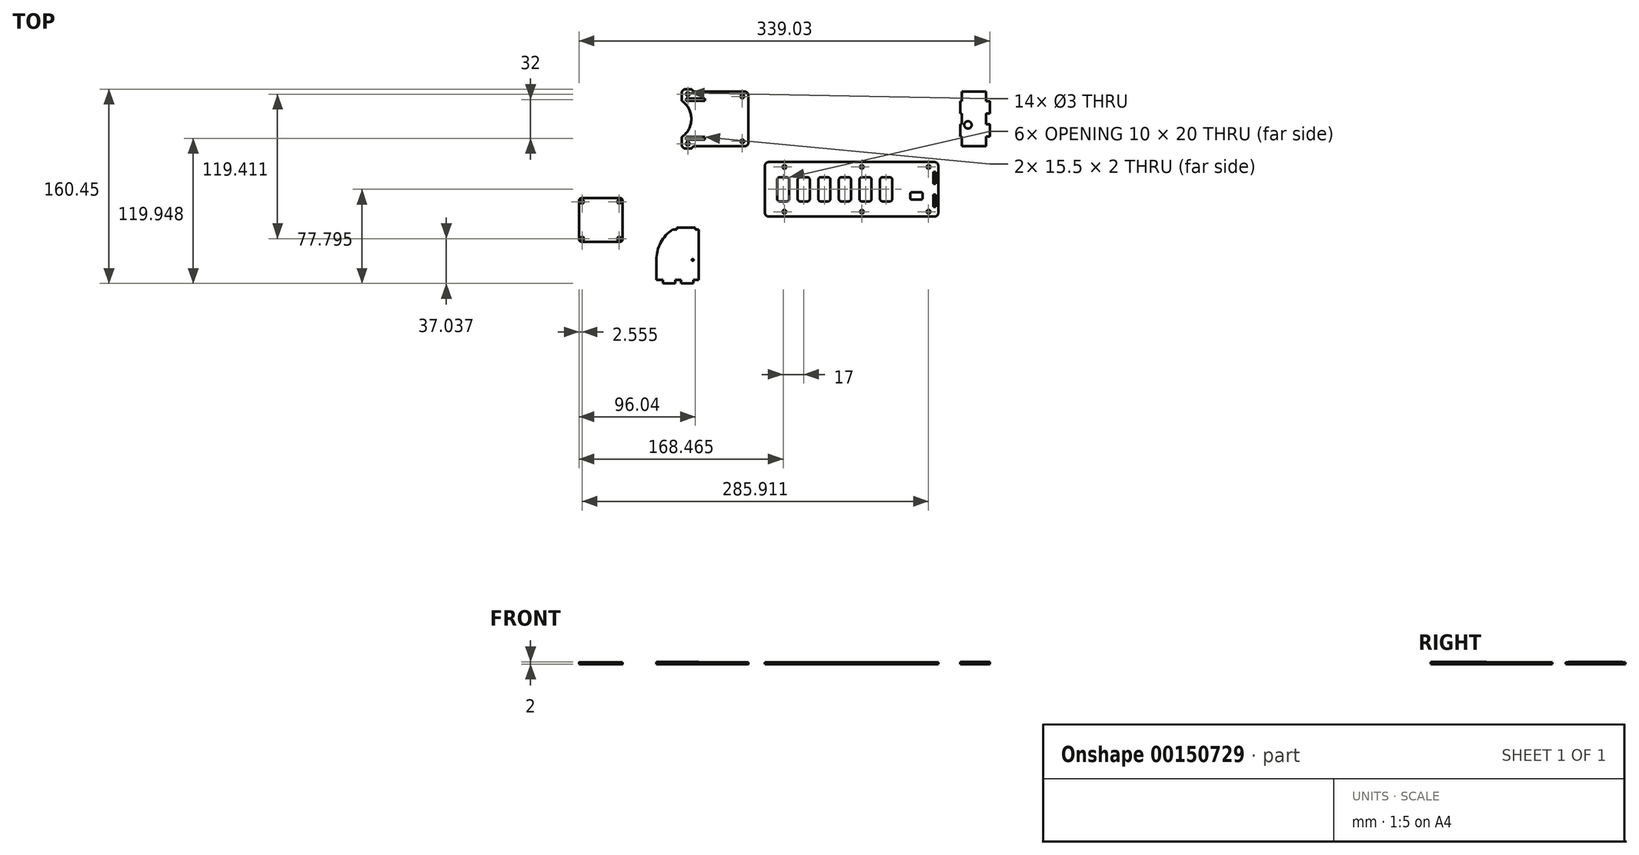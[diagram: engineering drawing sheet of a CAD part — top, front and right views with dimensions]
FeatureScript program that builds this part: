
annotation { "Feature Type Name" : "Feature", "Feature Type Description" : "" }
export const myFeature = defineFeature(function(context is Context, id is Id, definition is map)
    precondition{}
    {
        {
            var Q0;
            Q0=qCreatedBy(makeId("Top.planeOp"),FACE);
            var sketch = newSketch(context, id + "F0", { "sketchPlane" : qUnion([Q0])});
            skLineSegment(sketch, "E0", {"start": v(29.73, 71.96) * mm, "end": v(20.47, 71.96) * mm, "construction": true});
            skPoint(sketch, "E0.startSnap0", {"position": v(35, 71.96) * mm});
            skLineSegment(sketch, "E1.bottom", {"start": v(-69.79, 6.5) * mm, "end": v(-37.79, 6.5) * mm});
            skLineSegment(sketch, "E1.top", {"start": v(-69.79, -29.5) * mm, "end": v(-37.79, -29.5) * mm});
            skLineSegment(sketch, "E1.left", {"start": v(-71.79, 4.5) * mm, "end": v(-71.79, -27.5) * mm});
            skLineSegment(sketch, "E1.right", {"start": v(-35.79, 4.5) * mm, "end": v(-35.79, -27.5) * mm});
            skLineSegment(sketch, "E2.bottom", {"start": v(-69.24, 3.55) * mm, "end": v(-38.74, 3.55) * mm, "construction": true});
            skLineSegment(sketch, "E2.top", {"start": v(-69.24, -26.95) * mm, "end": v(-38.74, -26.95) * mm, "construction": true});
            skLineSegment(sketch, "E2.left", {"start": v(-69.24, 3.55) * mm, "end": v(-69.24, -26.95) * mm, "construction": true});
            skLineSegment(sketch, "E2.right", {"start": v(-38.74, 3.55) * mm, "end": v(-38.74, -26.95) * mm, "construction": true});
            skCircle(sketch, "E3", {"center": v(-69.24, 3.55) * mm, "radius": 1.5 * mm});
            skCircle(sketch, "E4", {"center": v(-38.74, 3.55) * mm, "radius": 1.5 * mm});
            skCircle(sketch, "E5", {"center": v(-38.74, -26.95) * mm, "radius": 1.5 * mm});
            skCircle(sketch, "E6", {"center": v(-69.24, -26.95) * mm, "radius": 1.5 * mm});
            skPoint(sketch, "E7.visualSharp", {"position": v(-71.79, 6.5) * mm});
            skArc(sketch, "E7.filletArc", {"start": v(-69.79, 6.5) * mm, "mid": v(-71.2, 5.91) * mm, "end": v(-71.79, 4.5) * mm});
            skPoint(sketch, "E8.visualSharp", {"position": v(-35.79, 6.5) * mm});
            skArc(sketch, "E8.filletArc", {"start": v(-35.79, 4.5) * mm, "mid": v(-36.37, 5.91) * mm, "end": v(-37.79, 6.5) * mm});
            skPoint(sketch, "E9.visualSharp", {"position": v(-35.79, -29.5) * mm});
            skArc(sketch, "E9.filletArc", {"start": v(-37.79, -29.5) * mm, "mid": v(-36.37, -28.92) * mm, "end": v(-35.79, -27.5) * mm});
            skPoint(sketch, "E10.visualSharp", {"position": v(-71.79, -29.5) * mm});
            skArc(sketch, "E10.filletArc", {"start": v(-71.79, -27.5) * mm, "mid": v(-71.2, -28.92) * mm, "end": v(-69.79, -29.5) * mm});
            skLineSegment(sketch, "E11", {"start": v(32, 54.96) * mm, "end": v(16.5, 54.96) * mm});
            skLineSegment(sketch, "E12", {"start": v(16.5, 54.96) * mm, "end": v(16.5, 56.96) * mm});
            skLineSegment(sketch, "E13", {"start": v(16.5, 56.96) * mm, "end": v(32, 56.96) * mm});
            skLineSegment(sketch, "E14", {"start": v(32, 56.96) * mm, "end": v(32, 54.96) * mm});
            skLineSegment(sketch, "E15.MirrorCS", {"start": v(32, 86.96) * mm, "end": v(32, 88.96) * mm});
            skLineSegment(sketch, "E16.MirrorCS", {"start": v(16.5, 86.96) * mm, "end": v(32, 86.96) * mm});
            skLineSegment(sketch, "E17.MirrorCS", {"start": v(16.5, 88.96) * mm, "end": v(16.5, 86.96) * mm});
            skLineSegment(sketch, "E18.MirrorCS", {"start": v(32, 88.96) * mm, "end": v(16.5, 88.96) * mm});
            skLineSegment(sketch, "E19", {"start": v(13, 94.46) * mm, "end": v(13, 86.96) * mm});
            skLineSegment(sketch, "E20", {"start": v(13, 49.46) * mm, "end": v(13, 56.96) * mm});
            skArc(sketch, "E21", {"start": v(13, 56.96) * mm, "mid": v(20.87, 71.96) * mm, "end": v(13, 86.96) * mm});
            skLineSegment(sketch, "E22.bottom", {"start": v(244.24, 94.46) * mm, "end": v(264.24, 94.46) * mm});
            skLineSegment(sketch, "E22.top", {"start": v(244.24, 49.46) * mm, "end": v(264.24, 49.46) * mm});
            skLineSegment(sketch, "E22.left", {"start": v(244.24, 94.46) * mm, "end": v(244.24, 49.46) * mm});
            skLineSegment(sketch, "E22.right", {"start": v(264.24, 94.46) * mm, "end": v(264.24, 49.46) * mm});
            skLineSegment(sketch, "E23", {"start": v(244.24, 86.46) * mm, "end": v(242.74, 86.46) * mm});
            skLineSegment(sketch, "E24", {"start": v(242.74, 57.46) * mm, "end": v(244.24, 57.46) * mm});
            skLineSegment(sketch, "E25", {"start": v(254.24, 80.62) * mm, "end": v(254.24, 71.6) * mm, "construction": true});
            skPoint(sketch, "E25.startSnap0", {"position": v(254.24, 94.46) * mm});
            skLineSegment(sketch, "E26", {"start": v(252.37, 71.96) * mm, "end": v(257.45, 71.96) * mm, "construction": true});
            skPoint(sketch, "E26.startSnap0", {"position": v(244.24, 71.96) * mm});
            skCircle(sketch, "E27", {"center": v(249.24, 66.96) * mm, "radius": 3.05 * mm});
            skLineSegment(sketch, "E28", {"start": v(242.74, 86.46) * mm, "end": v(242.74, 76.46) * mm});
            skLineSegment(sketch, "E29", {"start": v(242.74, 76.46) * mm, "end": v(244.24, 76.46) * mm});
            skLineSegment(sketch, "E30", {"start": v(242.74, 57.46) * mm, "end": v(242.74, 67.46) * mm});
            skLineSegment(sketch, "E31", {"start": v(242.74, 67.46) * mm, "end": v(244.24, 67.46) * mm});
            skLineSegment(sketch, "E32", {"start": v(264.24, 86.46) * mm, "end": v(267.24, 86.46) * mm});
            skPoint(sketch, "E33.endSnap0", {"position": v(254.24, 76.11) * mm});
            skLineSegment(sketch, "E34", {"start": v(264.24, 76.46) * mm, "end": v(267.24, 76.46) * mm});
            skLineSegment(sketch, "E35", {"start": v(267.24, 76.46) * mm, "end": v(267.24, 86.46) * mm});
            skLineSegment(sketch, "E36.MirrorCS", {"start": v(264.24, 57.46) * mm, "end": v(267.24, 57.46) * mm});
            skLineSegment(sketch, "E37.MirrorCS", {"start": v(267.24, 67.46) * mm, "end": v(267.24, 57.46) * mm});
            skLineSegment(sketch, "E38.MirrorCS", {"start": v(264.24, 67.46) * mm, "end": v(267.24, 67.46) * mm});
            skLineSegment(sketch, "E39.right", {"start": v(224.68, 33.3) * mm, "end": v(224.68, -5.7) * mm});
            skLineSegment(sketch, "E40", {"start": v(84.68, 36.3) * mm, "end": v(221.68, 36.3) * mm});
            skLineSegment(sketch, "E41", {"start": v(221.68, -8.7) * mm, "end": v(84.68, -8.7) * mm});
            skCircle(sketch, "E42", {"center": v(97.68, 32.3) * mm, "radius": 1.5 * mm});
            skPoint(sketch, "E43.visualSharp", {"position": v(224.68, 36.3) * mm});
            skArc(sketch, "E43.filletArc", {"start": v(224.68, 33.3) * mm, "mid": v(223.8, 35.43) * mm, "end": v(221.68, 36.3) * mm});
            skPoint(sketch, "E44.visualSharp", {"position": v(224.68, -8.7) * mm});
            skArc(sketch, "E44.filletArc", {"start": v(221.68, -8.7) * mm, "mid": v(223.8, -7.82) * mm, "end": v(224.68, -5.7) * mm});
            skCircle(sketch, "E45.MirrorC", {"center": v(97.68, -4.7) * mm, "radius": 1.5 * mm});
            skLineSegment(sketch, "E46.bottom", {"start": v(93.68, 23.8) * mm, "end": v(99.68, 23.8) * mm});
            skLineSegment(sketch, "E46.top", {"start": v(93.68, 3.8) * mm, "end": v(99.68, 3.8) * mm});
            skLineSegment(sketch, "E46.left", {"start": v(91.68, 21.8) * mm, "end": v(91.68, 5.8) * mm});
            skLineSegment(sketch, "E46.right", {"start": v(101.68, 21.8) * mm, "end": v(101.68, 5.8) * mm});
            skPoint(sketch, "E47.visualSharp", {"position": v(91.68, 23.8) * mm});
            skArc(sketch, "E47.filletArc", {"start": v(93.68, 23.8) * mm, "mid": v(92.26, 23.22) * mm, "end": v(91.68, 21.8) * mm});
            skPoint(sketch, "E48.visualSharp", {"position": v(101.68, 23.8) * mm});
            skArc(sketch, "E48.filletArc", {"start": v(101.68, 21.8) * mm, "mid": v(101.09, 23.22) * mm, "end": v(99.68, 23.8) * mm});
            skPoint(sketch, "E49.visualSharp", {"position": v(101.68, 3.8) * mm});
            skArc(sketch, "E49.filletArc", {"start": v(99.68, 3.8) * mm, "mid": v(101.09, 4.4) * mm, "end": v(101.68, 5.8) * mm});
            skPoint(sketch, "E50.visualSharp", {"position": v(91.68, 3.8) * mm});
            skArc(sketch, "E50.filletArc", {"start": v(91.68, 5.8) * mm, "mid": v(92.26, 4.4) * mm, "end": v(93.68, 3.8) * mm});
            skLineSegment(sketch, "E51.1.0.0", {"start": v(110.68, 23.8) * mm, "end": v(116.68, 23.8) * mm});
            skPoint(sketch, "E51.1.0.1", {"position": v(118.68, 23.8) * mm});
            skPoint(sketch, "E51.1.0.2", {"position": v(108.68, 3.8) * mm});
            skPoint(sketch, "E51.1.0.3", {"position": v(118.68, 3.8) * mm});
            skLineSegment(sketch, "E51.1.0.4", {"start": v(110.68, 3.8) * mm, "end": v(116.68, 3.8) * mm});
            skLineSegment(sketch, "E51.1.0.5", {"start": v(108.68, 21.8) * mm, "end": v(108.68, 5.8) * mm});
            skPoint(sketch, "E51.1.0.6", {"position": v(108.68, 23.8) * mm});
            skLineSegment(sketch, "E51.1.0.7", {"start": v(118.68, 21.8) * mm, "end": v(118.68, 5.8) * mm});
            skArc(sketch, "E51.1.0.8", {"start": v(110.68, 23.8) * mm, "mid": v(109.26, 23.22) * mm, "end": v(108.68, 21.8) * mm});
            skArc(sketch, "E51.1.0.9", {"start": v(118.68, 21.8) * mm, "mid": v(118.09, 23.22) * mm, "end": v(116.68, 23.8) * mm});
            skArc(sketch, "E51.1.0.10", {"start": v(116.68, 3.8) * mm, "mid": v(118.09, 4.4) * mm, "end": v(118.68, 5.8) * mm});
            skArc(sketch, "E51.1.0.11", {"start": v(108.68, 5.8) * mm, "mid": v(109.26, 4.4) * mm, "end": v(110.68, 3.8) * mm});
            skLineSegment(sketch, "E51.2.0.0", {"start": v(127.68, 23.8) * mm, "end": v(133.68, 23.8) * mm});
            skPoint(sketch, "E51.2.0.1", {"position": v(135.68, 23.8) * mm});
            skPoint(sketch, "E51.2.0.2", {"position": v(125.68, 3.8) * mm});
            skPoint(sketch, "E51.2.0.3", {"position": v(135.68, 3.8) * mm});
            skLineSegment(sketch, "E51.2.0.4", {"start": v(127.68, 3.8) * mm, "end": v(133.68, 3.8) * mm});
            skLineSegment(sketch, "E51.2.0.5", {"start": v(125.68, 21.8) * mm, "end": v(125.68, 5.8) * mm});
            skPoint(sketch, "E51.2.0.6", {"position": v(125.68, 23.8) * mm});
            skLineSegment(sketch, "E51.2.0.7", {"start": v(135.68, 21.8) * mm, "end": v(135.68, 5.8) * mm});
            skArc(sketch, "E51.2.0.8", {"start": v(127.68, 23.8) * mm, "mid": v(126.26, 23.22) * mm, "end": v(125.68, 21.8) * mm});
            skArc(sketch, "E51.2.0.9", {"start": v(135.68, 21.8) * mm, "mid": v(135.09, 23.22) * mm, "end": v(133.68, 23.8) * mm});
            skArc(sketch, "E51.2.0.10", {"start": v(133.68, 3.8) * mm, "mid": v(135.09, 4.4) * mm, "end": v(135.68, 5.8) * mm});
            skArc(sketch, "E51.2.0.11", {"start": v(125.68, 5.8) * mm, "mid": v(126.26, 4.4) * mm, "end": v(127.68, 3.8) * mm});
            skLineSegment(sketch, "E51.3.0.0", {"start": v(144.68, 23.8) * mm, "end": v(150.68, 23.8) * mm});
            skPoint(sketch, "E51.3.0.1", {"position": v(152.68, 23.8) * mm});
            skPoint(sketch, "E51.3.0.2", {"position": v(142.68, 3.8) * mm});
            skPoint(sketch, "E51.3.0.3", {"position": v(152.68, 3.8) * mm});
            skLineSegment(sketch, "E51.3.0.4", {"start": v(144.68, 3.8) * mm, "end": v(150.68, 3.8) * mm});
            skLineSegment(sketch, "E51.3.0.5", {"start": v(142.68, 21.8) * mm, "end": v(142.68, 5.8) * mm});
            skPoint(sketch, "E51.3.0.6", {"position": v(142.68, 23.8) * mm});
            skLineSegment(sketch, "E51.3.0.7", {"start": v(152.68, 21.8) * mm, "end": v(152.68, 5.8) * mm});
            skArc(sketch, "E51.3.0.8", {"start": v(144.68, 23.8) * mm, "mid": v(143.26, 23.22) * mm, "end": v(142.68, 21.8) * mm});
            skArc(sketch, "E51.3.0.9", {"start": v(152.68, 21.8) * mm, "mid": v(152.09, 23.22) * mm, "end": v(150.68, 23.8) * mm});
            skArc(sketch, "E51.3.0.10", {"start": v(150.68, 3.8) * mm, "mid": v(152.09, 4.4) * mm, "end": v(152.68, 5.8) * mm});
            skArc(sketch, "E51.3.0.11", {"start": v(142.68, 5.8) * mm, "mid": v(143.26, 4.4) * mm, "end": v(144.68, 3.8) * mm});
            skLineSegment(sketch, "E51.4.0.0", {"start": v(161.68, 23.8) * mm, "end": v(167.68, 23.8) * mm});
            skPoint(sketch, "E51.4.0.1", {"position": v(169.68, 23.8) * mm});
            skPoint(sketch, "E51.4.0.2", {"position": v(159.68, 3.8) * mm});
            skPoint(sketch, "E51.4.0.3", {"position": v(169.68, 3.8) * mm});
            skLineSegment(sketch, "E51.4.0.4", {"start": v(161.68, 3.8) * mm, "end": v(167.68, 3.8) * mm});
            skLineSegment(sketch, "E51.4.0.5", {"start": v(159.68, 21.8) * mm, "end": v(159.68, 5.8) * mm});
            skPoint(sketch, "E51.4.0.6", {"position": v(159.68, 23.8) * mm});
            skLineSegment(sketch, "E51.4.0.7", {"start": v(169.68, 21.8) * mm, "end": v(169.68, 5.8) * mm});
            skArc(sketch, "E51.4.0.8", {"start": v(161.68, 23.8) * mm, "mid": v(160.26, 23.22) * mm, "end": v(159.68, 21.8) * mm});
            skArc(sketch, "E51.4.0.9", {"start": v(169.68, 21.8) * mm, "mid": v(169.09, 23.22) * mm, "end": v(167.68, 23.8) * mm});
            skArc(sketch, "E51.4.0.10", {"start": v(167.68, 3.8) * mm, "mid": v(169.09, 4.4) * mm, "end": v(169.68, 5.8) * mm});
            skArc(sketch, "E51.4.0.11", {"start": v(159.68, 5.8) * mm, "mid": v(160.26, 4.4) * mm, "end": v(161.68, 3.8) * mm});
            skLineSegment(sketch, "E51.5.0.0", {"start": v(178.68, 23.8) * mm, "end": v(184.68, 23.8) * mm});
            skPoint(sketch, "E51.5.0.1", {"position": v(186.68, 23.8) * mm});
            skPoint(sketch, "E51.5.0.2", {"position": v(176.68, 3.8) * mm});
            skPoint(sketch, "E51.5.0.3", {"position": v(186.68, 3.8) * mm});
            skLineSegment(sketch, "E51.5.0.4", {"start": v(178.68, 3.8) * mm, "end": v(184.68, 3.8) * mm});
            skLineSegment(sketch, "E51.5.0.5", {"start": v(176.68, 21.8) * mm, "end": v(176.68, 5.8) * mm});
            skPoint(sketch, "E51.5.0.6", {"position": v(176.68, 23.8) * mm});
            skLineSegment(sketch, "E51.5.0.7", {"start": v(186.68, 21.8) * mm, "end": v(186.68, 5.8) * mm});
            skArc(sketch, "E51.5.0.8", {"start": v(178.68, 23.8) * mm, "mid": v(177.26, 23.22) * mm, "end": v(176.68, 21.8) * mm});
            skArc(sketch, "E51.5.0.9", {"start": v(186.68, 21.8) * mm, "mid": v(186.09, 23.22) * mm, "end": v(184.68, 23.8) * mm});
            skArc(sketch, "E51.5.0.10", {"start": v(184.68, 3.8) * mm, "mid": v(186.09, 4.4) * mm, "end": v(186.68, 5.8) * mm});
            skArc(sketch, "E51.5.0.11", {"start": v(176.68, 5.8) * mm, "mid": v(177.26, 4.4) * mm, "end": v(178.68, 3.8) * mm});
            skLineSegment(sketch, "E51.direction1", {"start": v(91.68, 3.8) * mm, "end": v(108.68, 3.8) * mm, "construction": true});
            skLineSegment(sketch, "E52", {"start": v(222.68, 28.3) * mm, "end": v(220.68, 28.3) * mm});
            skLineSegment(sketch, "E53", {"start": v(220.68, -0.7) * mm, "end": v(222.68, -0.7) * mm});
            skLineSegment(sketch, "E54", {"start": v(220.68, 28.3) * mm, "end": v(220.68, 18.3) * mm});
            skLineSegment(sketch, "E55", {"start": v(220.68, 18.3) * mm, "end": v(222.68, 18.3) * mm});
            skLineSegment(sketch, "E56", {"start": v(222.68, 18.3) * mm, "end": v(222.68, 28.3) * mm});
            skLineSegment(sketch, "E57", {"start": v(220.68, -0.7) * mm, "end": v(220.68, 9.3) * mm});
            skLineSegment(sketch, "E58", {"start": v(220.68, 9.3) * mm, "end": v(222.68, 9.3) * mm});
            skLineSegment(sketch, "E59", {"start": v(222.68, 9.3) * mm, "end": v(222.68, -0.7) * mm});
            skCircle(sketch, "E60", {"center": v(216.68, 32.3) * mm, "radius": 1.5 * mm});
            skCircle(sketch, "E61.MirrorC", {"center": v(216.68, -4.7) * mm, "radius": 1.5 * mm});
            skCircle(sketch, "E62", {"center": v(161.68, 32.3) * mm, "radius": 1.5 * mm});
            skLineSegment(sketch, "E63", {"start": v(81.68, 33.3) * mm, "end": v(81.68, -5.7) * mm});
            skPoint(sketch, "E64.visualSharp", {"position": v(81.68, 36.3) * mm});
            skArc(sketch, "E64.filletArc", {"start": v(84.68, 36.3) * mm, "mid": v(82.55, 35.43) * mm, "end": v(81.68, 33.3) * mm});
            skPoint(sketch, "E65.visualSharp", {"position": v(81.68, -8.7) * mm});
            skArc(sketch, "E65.filletArc", {"start": v(81.68, -5.7) * mm, "mid": v(82.55, -7.82) * mm, "end": v(84.68, -8.7) * mm});
            skCircle(sketch, "E66.MirrorC", {"center": v(161.68, -4.7) * mm, "radius": 1.5 * mm});
            skLineSegment(sketch, "E67", {"start": v(68, 91.46) * mm, "end": v(68, 52.46) * mm});
            skLineSegment(sketch, "E68", {"start": v(65, 49.46) * mm, "end": v(23, 49.46) * mm});
            skCircle(sketch, "E69", {"center": v(63, 90.46) * mm, "radius": 1.5 * mm});
            skCircle(sketch, "E70.MirrorC", {"center": v(63, 53.46) * mm, "radius": 1.5 * mm});
            skPoint(sketch, "E71.visualSharp", {"position": v(68, 94.46) * mm});
            skArc(sketch, "E71.filletArc", {"start": v(68, 91.46) * mm, "mid": v(67.12, 93.58) * mm, "end": v(65, 94.46) * mm});
            skPoint(sketch, "E72.visualSharp", {"position": v(68, 49.46) * mm});
            skArc(sketch, "E72.filletArc", {"start": v(65, 49.46) * mm, "mid": v(67.12, 50.34) * mm, "end": v(68, 52.46) * mm});
            skLineSegment(sketch, "E73", {"start": v(-7.98, -61) * mm, "end": v(27.02, -61) * mm});
            skLineSegment(sketch, "E74", {"start": v(27.02, -61) * mm, "end": v(27.02, -19.5) * mm});
            skLineSegment(sketch, "E75", {"start": v(-7.98, -44.5) * mm, "end": v(-7.98, -61) * mm});
            skLineSegment(sketch, "E76", {"start": v(-2.48, -61) * mm, "end": v(-2.48, -64) * mm});
            skLineSegment(sketch, "E77", {"start": v(-2.48, -64) * mm, "end": v(7.52, -64) * mm});
            skLineSegment(sketch, "E78", {"start": v(7.52, -64) * mm, "end": v(7.52, -61) * mm});
            skLineSegment(sketch, "E79", {"start": v(12.52, -61) * mm, "end": v(12.52, -64) * mm});
            skLineSegment(sketch, "E80", {"start": v(12.52, -64) * mm, "end": v(22.52, -64) * mm});
            skLineSegment(sketch, "E81", {"start": v(22.52, -64) * mm, "end": v(22.52, -61) * mm});
            skCircle(sketch, "E82", {"center": v(22.02, -44.5) * mm, "radius": 0.75 * mm});
            skLineSegment(sketch, "E83", {"start": v(5.43, -19.5) * mm, "end": v(27.02, -19.5) * mm});
            skLineSegment(sketch, "E84", {"start": v(9.02, -19.5) * mm, "end": v(9.02, -18) * mm});
            skLineSegment(sketch, "E85", {"start": v(9.02, -18) * mm, "end": v(24.02, -18) * mm});
            skLineSegment(sketch, "E86", {"start": v(24.02, -18) * mm, "end": v(24.02, -19.5) * mm});
            skLineSegment(sketch, "E87", {"start": v(7.52, -59.08) * mm, "end": v(12.52, -59.08) * mm, "construction": true});
            skPoint(sketch, "E87.endSnap0", {"position": v(12.52, -62.5) * mm});
            skLineSegment(sketch, "E88", {"start": v(10.02, -59.08) * mm, "end": v(10.02, -55.43) * mm, "construction": true});
            skArc(sketch, "E89", {"start": v(-7.98, -44.5) * mm, "mid": v(-4.42, -30.3) * mm, "end": v(5.43, -19.5) * mm});
            skCircle(sketch, "E90", {"center": v(18, 51.46) * mm, "radius": 1.5 * mm});
            skLineSegment(sketch, "E91", {"start": v(15.41, 47.46) * mm, "end": v(20.59, 47.46) * mm});
            skLineSegment(sketch, "E92", {"start": v(14.7, 47.75) * mm, "end": v(13, 49.46) * mm});
            skLineSegment(sketch, "E93", {"start": v(21.3, 47.75) * mm, "end": v(23, 49.46) * mm});
            skPoint(sketch, "E94.visualSharp", {"position": v(15, 47.46) * mm});
            skArc(sketch, "E94.filletArc", {"start": v(14.7, 47.75) * mm, "mid": v(15.03, 47.53) * mm, "end": v(15.41, 47.46) * mm});
            skPoint(sketch, "E95.visualSharp", {"position": v(21, 47.46) * mm});
            skArc(sketch, "E95.filletArc", {"start": v(20.59, 47.46) * mm, "mid": v(20.97, 47.53) * mm, "end": v(21.3, 47.75) * mm});
            skLineSegment(sketch, "E96.MirrorCS", {"start": v(14.7, 96.17) * mm, "end": v(13, 94.46) * mm});
            skLineSegment(sketch, "E97.MirrorCS", {"start": v(15.41, 96.46) * mm, "end": v(20.59, 96.46) * mm});
            skArc(sketch, "E98.MirrorCS", {"start": v(14.7, 96.17) * mm, "mid": v(15.03, 96.38) * mm, "end": v(15.41, 96.46) * mm});
            skArc(sketch, "E99.MirrorCS", {"start": v(20.59, 96.46) * mm, "mid": v(20.97, 96.38) * mm, "end": v(21.3, 96.17) * mm});
            skLineSegment(sketch, "E100.MirrorCS", {"start": v(65, 94.46) * mm, "end": v(23, 94.46) * mm});
            skLineSegment(sketch, "E101.MirrorCS", {"start": v(21.3, 96.17) * mm, "end": v(23, 94.46) * mm});
            skCircle(sketch, "E102.MirrorC", {"center": v(18, 92.46) * mm, "radius": 1.5 * mm});
            skPoint(sketch, "E103.visualSharp", {"position": v(210.2, 3.8) * mm});
            skPoint(sketch, "E104.visualSharp", {"position": v(210.2, 9.43) * mm});
            skLineSegment(sketch, "E105", {"start": v(211.68, 6.3) * mm, "end": v(211.68, 10.3) * mm});
            skLineSegment(sketch, "E106", {"start": v(210.68, 11.3) * mm, "end": v(202.68, 11.3) * mm});
            skLineSegment(sketch, "E107", {"start": v(201.68, 10.3) * mm, "end": v(201.68, 6.3) * mm});
            skLineSegment(sketch, "E108", {"start": v(202.68, 5.3) * mm, "end": v(210.68, 5.3) * mm});
            skLineSegment(sketch, "E109", {"start": v(215.28, 13.8) * mm, "end": v(212.6, 13.8) * mm, "construction": true});
            skPoint(sketch, "E109.startSnap0", {"position": v(224.68, 13.8) * mm});
            skPoint(sketch, "E110.visualSharp", {"position": v(201.68, 11.3) * mm});
            skArc(sketch, "E110.filletArc", {"start": v(202.68, 11.3) * mm, "mid": v(201.97, 11.01) * mm, "end": v(201.68, 10.3) * mm});
            skPoint(sketch, "E111.visualSharp", {"position": v(201.68, 5.3) * mm});
            skArc(sketch, "E111.filletArc", {"start": v(201.68, 6.3) * mm, "mid": v(201.97, 5.6) * mm, "end": v(202.68, 5.3) * mm});
            skPoint(sketch, "E112.visualSharp", {"position": v(211.68, 5.3) * mm});
            skArc(sketch, "E112.filletArc", {"start": v(210.68, 5.3) * mm, "mid": v(211.38, 5.6) * mm, "end": v(211.68, 6.3) * mm});
            skPoint(sketch, "E113.visualSharp", {"position": v(211.68, 11.3) * mm});
            skArc(sketch, "E113.filletArc", {"start": v(211.68, 10.3) * mm, "mid": v(211.38, 11.01) * mm, "end": v(210.68, 11.3) * mm});
            skSolve(sketch);
        }
        {
            var Q0;
            Q0=makeQuery(id+"F0.imprint","IMPRINT",FACE,{"disambiguationData":[TD([[makeQuery(id+"F0.imprint","IMPRINT",EDGE,{"derivedFrom":sQuery(id+"F0.wireOp",EDGE,"E11")}),1.0]])]});
            var Q1;
            {var subQ5=sQuery(id+"F0.wireOp",EDGE,"91yZrbAR-TbWA-sJQh-pMqF-KEnHeWjptpjc");Q1=makeQuery(id+"F0.imprint","IMPRINT",FACE,{"disambiguationData":[TD([[makeQuery(id+"F0.imprint","IMPRINT",EDGE,{"derivedFrom":subQ5}),1.0]])]});}
            var Q2;
            {var subQ0=sQuery(id+"F0.wireOp",EDGE,"Oo2yq7zO-nwMB-Ah5b-oMXD-a6HD9qoYs4ca");Q2=makeQuery(id+"F0.imprint","IMPRINT",FACE,{"disambiguationData":[TD([[makeQuery(id+"F0.imprint","IMPRINT",EDGE,{"derivedFrom":subQ0}),-1.0]])]});}
            var Q3;
            {var subQ0=sQuery(id+"F0.wireOp",EDGE,"T9HIJzcP-D60b-KIGM-pP6u-N85cowEV2lf5");Q3=makeQuery(id+"F0.imprint","IMPRINT",FACE,{"disambiguationData":[TD([[makeQuery(id+"F0.imprint","IMPRINT",EDGE,{"derivedFrom":subQ0}),1.0]])]});}
            var Q4;
            {var subQ0=sQuery(id+"F0.wireOp",EDGE,"pDNolIKI-n5qm-4BI0-PvBm-unxkYONWWrE6");Q4=makeQuery(id+"F0.imprint","IMPRINT",FACE,{"disambiguationData":[TD([[makeQuery(id+"F0.imprint","IMPRINT",EDGE,{"derivedFrom":subQ0}),1.0]])]});}
            var Q5;
            Q5=makeQuery(id+"F0.imprint","IMPRINT",FACE,{"disambiguationData":[TD([[makeQuery(id+"F0.imprint","IMPRINT",EDGE,{"derivedFrom":sQuery(id+"F0.wireOp",EDGE,"E1.bottom")}),-1.0]])]});
            var Q6;
            Q6=makeQuery(id+"F0.imprint","IMPRINT",FACE,{"disambiguationData":[TD([[makeQuery(id+"F0.imprint","IMPRINT",EDGE,{"derivedFrom":sQuery(id+"F0.wireOp",EDGE,"E39.right")}),-1.0]])]});
            var Q7;
            {var subQ3=sQuery(id+"F0.wireOp",EDGE,"E22.bottom");Q7=makeQuery(id+"F0.imprint","IMPRINT",FACE,{"disambiguationData":[TD([[makeQuery(id+"F0.imprint","IMPRINT",EDGE,{"derivedFrom":subQ3}),-1.0]])]});}
            var Q8;
            {var subQ0=sQuery(id+"F0.wireOp",EDGE,"E32");Q8=makeQuery(id+"F0.imprint","IMPRINT",FACE,{"disambiguationData":[TD([[makeQuery(id+"F0.imprint","IMPRINT",EDGE,{"derivedFrom":subQ0}),-1.0]])]});}
            var Q9;
            {var subQ0=sQuery(id+"F0.wireOp",EDGE,"E36.MirrorCS");Q9=makeQuery(id+"F0.imprint","IMPRINT",FACE,{"disambiguationData":[TD([[makeQuery(id+"F0.imprint","IMPRINT",EDGE,{"derivedFrom":subQ0}),1.0]])]});}
            var Q10;
            {var subQ0=sQuery(id+"F0.wireOp",EDGE,"E24");Q10=makeQuery(id+"F0.imprint","IMPRINT",FACE,{"disambiguationData":[TD([[makeQuery(id+"F0.imprint","IMPRINT",EDGE,{"derivedFrom":subQ0}),1.0]])]});}
            var Q11;
            {var subQ0=sQuery(id+"F0.wireOp",EDGE,"E23");Q11=makeQuery(id+"F0.imprint","IMPRINT",FACE,{"disambiguationData":[TD([[makeQuery(id+"F0.imprint","IMPRINT",EDGE,{"derivedFrom":subQ0}),1.0]])]});}
            var Q12;
            {var subQ4=sQuery(id+"F0.wireOp",EDGE,"E74");Q12=makeQuery(id+"F0.imprint","IMPRINT",FACE,{"disambiguationData":[TD([[makeQuery(id+"F0.imprint","IMPRINT",EDGE,{"derivedFrom":subQ4}),1.0]])]});}
            var Q13;
            {var subQ0=sQuery(id+"F0.wireOp",EDGE,"E84");Q13=makeQuery(id+"F0.imprint","IMPRINT",FACE,{"disambiguationData":[TD([[makeQuery(id+"F0.imprint","IMPRINT",EDGE,{"derivedFrom":subQ0}),-1.0]])]});}
            var Q14;
            {var subQ0=sQuery(id+"F0.wireOp",EDGE,"E76");Q14=makeQuery(id+"F0.imprint","IMPRINT",FACE,{"disambiguationData":[TD([[makeQuery(id+"F0.imprint","IMPRINT",EDGE,{"derivedFrom":subQ0}),1.0]])]});}
            var Q15;
            {var subQ0=sQuery(id+"F0.wireOp",EDGE,"E79");Q15=makeQuery(id+"F0.imprint","IMPRINT",FACE,{"disambiguationData":[TD([[makeQuery(id+"F0.imprint","IMPRINT",EDGE,{"derivedFrom":subQ0}),1.0]])]});}
            extrude(context, id + "F1", {"entities" : qUnion([Q0, Q1, Q2, Q3, Q4, Q5, Q6, Q7, Q8, Q9, Q10, Q11, Q12, Q13, Q14, Q15]), "depth" : 1.5 * mm});
        }
        {
            var Q0;
            Q0=makeQuery(id+"F1.opExtrude","CAP_FACE",FACE,{"disambiguationData":[OSD([sQuery(id+"F0.wireOp",EDGE,"E73"),sQuery(id+"F0.wireOp",EDGE,"E74"),sQuery(id+"F0.wireOp",EDGE,"E75"),sQuery(id+"F0.wireOp",EDGE,"E76"),sQuery(id+"F0.wireOp",EDGE,"E77"),sQuery(id+"F0.wireOp",EDGE,"E78"),sQuery(id+"F0.wireOp",EDGE,"E79"),sQuery(id+"F0.wireOp",EDGE,"E80"),sQuery(id+"F0.wireOp",EDGE,"E81"),sQuery(id+"F0.wireOp",EDGE,"E82"),sQuery(id+"F0.wireOp",EDGE,"E83"),sQuery(id+"F0.wireOp",EDGE,"E84"),sQuery(id+"F0.wireOp",EDGE,"E85"),sQuery(id+"F0.wireOp",EDGE,"E86"),sQuery(id+"F0.wireOp",EDGE,"E89")])],"isStart":false});
            var Q1;
            Q1=makeQuery(id+"F1.opExtrude","CAP_FACE",FACE,{"disambiguationData":[OSD([sQuery(id+"F0.wireOp",EDGE,"E22.bottom"),sQuery(id+"F0.wireOp",EDGE,"E22.top"),sQuery(id+"F0.wireOp",EDGE,"E22.left"),sQuery(id+"F0.wireOp",EDGE,"E22.right"),sQuery(id+"F0.wireOp",EDGE,"E23"),sQuery(id+"F0.wireOp",EDGE,"E24"),sQuery(id+"F0.wireOp",EDGE,"E27"),sQuery(id+"F0.wireOp",EDGE,"E28"),sQuery(id+"F0.wireOp",EDGE,"E29"),sQuery(id+"F0.wireOp",EDGE,"E30"),sQuery(id+"F0.wireOp",EDGE,"E31"),sQuery(id+"F0.wireOp",EDGE,"E32"),sQuery(id+"F0.wireOp",EDGE,"E34"),sQuery(id+"F0.wireOp",EDGE,"E35"),sQuery(id+"F0.wireOp",EDGE,"E36.MirrorCS"),sQuery(id+"F0.wireOp",EDGE,"E37.MirrorCS"),sQuery(id+"F0.wireOp",EDGE,"E38.MirrorCS")])],"isStart":false});
            extrude(context, id + "F2", {"entities" : qUnion([Q0, Q1]), "operationType" : NewBodyOperationType.ADD, "depth" : 0.5 * mm});
        }
    });
